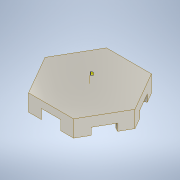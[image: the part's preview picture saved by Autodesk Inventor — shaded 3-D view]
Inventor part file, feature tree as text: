
AUTODESK INVENTOR PART (.ipt)
format: ipt  version: 2020 (Build 240168000, 168)  size: 696,832 bytes
history: native  units: mm
features: extrude x7, other x5, sketch x3, pattern_circular x1
ambient origin geometry x8: Origin, YZ Plane, XZ Plane, XY Plane, X Axis, Y Axis, Z Axis, Center Point
bodies: Body1 (feature_tree)
feature tree (16):
  sketch  "Sketch6"  dims[d72=6.5mm d85=1.0mm d86=0.0mm]
  extrude  "Fronte"  Depth=1.0mm TaperAngle=0.0deg
  extrude  "Esterno"  Depth=6.5mm
  extrude  "Strip"  Depth=2.0mm
  extrude  "Passacavi"  Depth=2.0mm
  extrude  "ScavoStrip"  Depth=26.0mm
  extrude  "SupportoViti"  Depth=2.5mm
  pattern_circular  "RipetizioneFori"  [2 undecoded]
  extrude  "Trasparenza"  TaperAngle=135.0deg  [1 undecoded]
  sketch  "Sketch7"  dims[d87=15.0mm d88=6.5mm]
  other  "Work Axis3"
  other  "Work Axis4"
  other  "Work Axis5"
  other  "Work Axis6"
  other  "Work Axis7"
  sketch  "Sketch11"  dims[d91=2.0mm d92=2.0mm d95=1.25mm d96=26.0mm d97=2.5mm d98=26.0mm d99=135.0deg d100=0.0mm d101=25.0mm d102=0.0mm d103=10.0mm d104=0.0mm d105=11.0mm d106=0.0mm d107=5.0mm d108=0.0mm d114=1.7mm d115=23.0mm d116=0.0mm d117=3.0mm d121=3.0mm d123=6.0mm d124=60.0mm d125=360.0deg d127=140.0mm d128=5.196152mm d129=5.196152mm d130=3.0mm d158=110.0mm d159=50.0mm d160=30.0mm d162=60.0mm d164=360.0deg d166=0.5mm d167=0.0mm d168=2.0mm]
note: 3 required parameter values undecoded (feature->parameter linkage not recoverable at this tier; creation-order binding heuristic only, values carry confidence <= 0.55)
